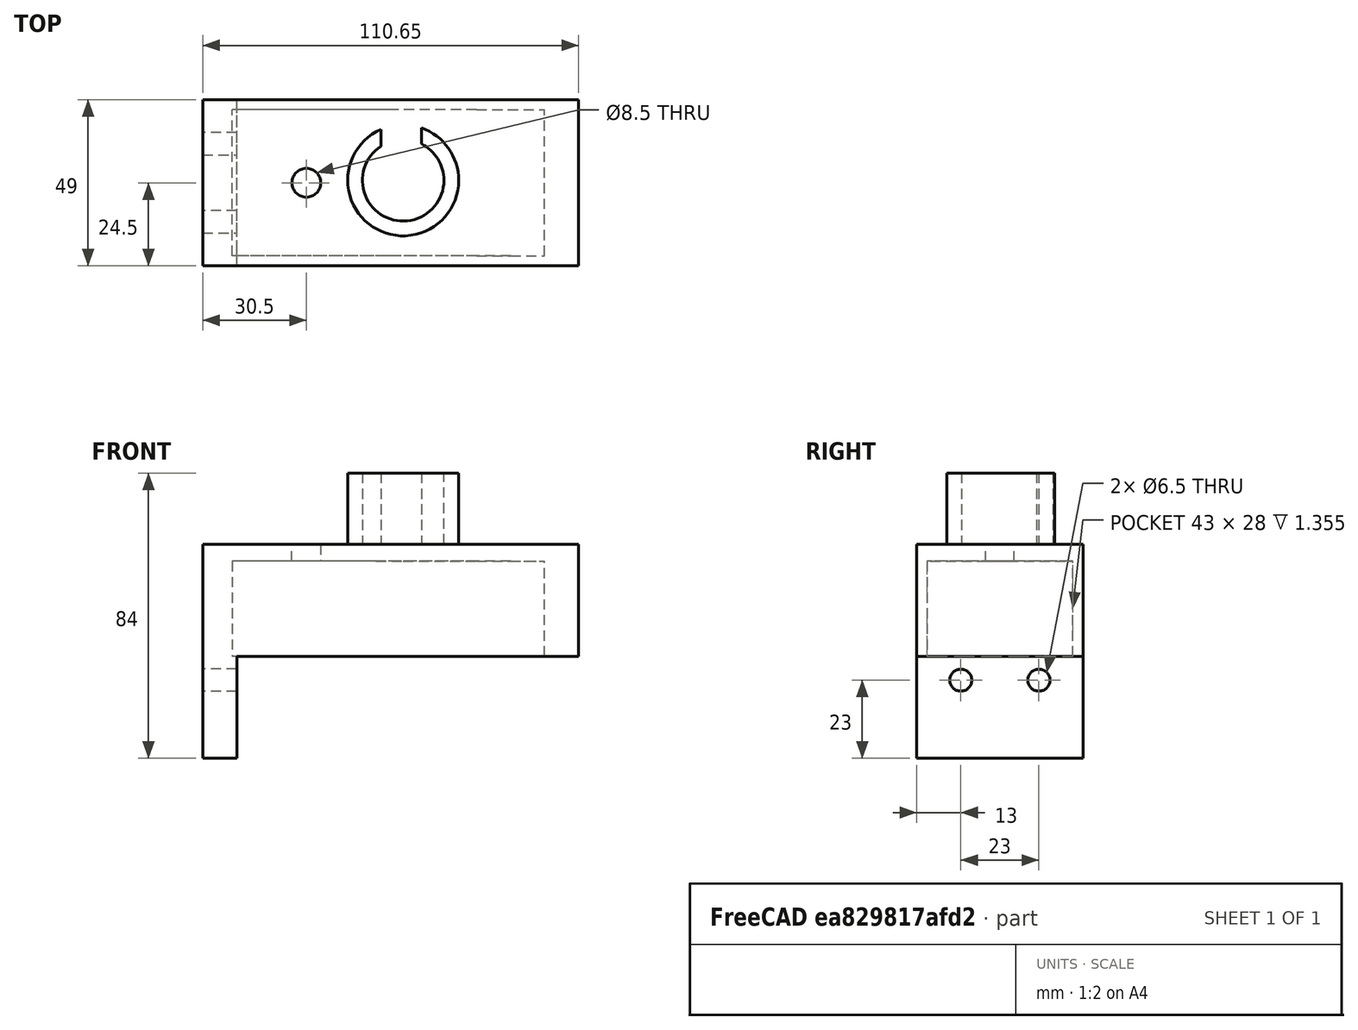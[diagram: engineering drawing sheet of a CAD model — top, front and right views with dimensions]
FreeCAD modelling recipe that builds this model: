
FCSTD DOCUMENT  (FreeCAD 0.18R4 (GitTag))
Label: Caja para engranes 1
License: All rights reserved
LicenseURL: http://en.wikipedia.org/wiki/All_rights_reserved
objects: Sketcher::SketchObject×23, PartDesign::Pad×9, PartDesign::Pocket×9, PartDesign::Body×1
note: 60 computed .brp shape members not serialized (recipe doc carries the construction recipe); baked Part::Feature solids carry a one-line shape summary decoded from their .brp

FEATURE [Sketcher::SketchObject] Sketch
  MapMode = 5
  Support = -> [XY_Plane]
  sketch-geometry (4):
    g0: LineSegment StartX=0 StartY=0 StartZ=0 EndX=49 EndY=0 EndZ=0
    g1: LineSegment StartX=49 StartY=0 StartZ=0 EndX=49 EndY=49 EndZ=0
    g2: LineSegment StartX=49 StartY=49 StartZ=0 EndX=0 EndY=49 EndZ=0
    g3: LineSegment StartX=0 StartY=49 StartZ=0 EndX=0 EndY=0 EndZ=0
  constraints (11):
    c: Coincident(g0,g1)
    c: Coincident(g1,g2)
    c: Coincident(g2,g3)
    c: Coincident(g3,g0)
    c: Horizontal(g0)
    c: Horizontal(g2)
    c: Vertical(g1)
    c: Vertical(g3)
    c: DistanceX(g0,g0) = 49
    c: DistanceY(g1,g1) = 49
    c: Coincident(g0,g-1)
FEATURE [PartDesign::Pad] Pad
  Length = 33
  Length2 = 100
  Profile = -> Sketch
  Type = 0
  expr: Length = 28 + 5
FEATURE [Sketcher::SketchObject] Sketch001
  ExternalGeometry = -> [Pad]
  MapMode = 5
  Placement = pos=(0,0,0) rot=(1,0,0;3.14159rad)
  Support = -> [Pad]
  sketch-geometry (6):
    g0: LineSegment StartX=45 StartY=-4 StartZ=0 EndX=4 EndY=-4 EndZ=0
    g1: LineSegment StartX=4 StartY=-4 StartZ=0 EndX=4 EndY=-45 EndZ=0
    g2: LineSegment StartX=4 StartY=-45 StartZ=0 EndX=45 EndY=-45 EndZ=0
    g3: LineSegment StartX=45 StartY=-45 StartZ=0 EndX=45 EndY=-4 EndZ=0
    g4: Circle [constr] CenterX=24.5 CenterY=-24.5 CenterZ=0 NormalX=0 NormalY=0 NormalZ=1 AngleXU=0 Radius=28.9914
    g5: Circle [constr] CenterX=24.5 CenterY=-24.5 CenterZ=0 NormalX=0 NormalY=0 NormalZ=1 AngleXU=0 Radius=34.6482
  constraints (17):
    c: Coincident(g0,g1)
    c: Coincident(g1,g2)
    c: Coincident(g2,g3)
    c: Coincident(g3,g0)
    c: Equal(g0,g1)
    c: Equal(g0,g2)
    c: Equal(g0,g3)
    c: PointOnObject(g0,g4)
    c: PointOnObject(g1,g4)
    c: PointOnObject(g2,g4)
    c: PointOnObject(g3,g4)
    c: Vertical(g3)
    c: DistanceX(g2,g2) = 41
    c: PointOnObject(g-4,g5)
    c: PointOnObject(g-3,g5)
    c: PointOnObject(g-1,g5)
    c: Coincident(g5,g4)
FEATURE [PartDesign::Pocket] Pocket
  BaseFeature = -> Pad
  Length = 28
  Length2 = 100
  Profile = -> Sketch001
  Type = 0
FEATURE [Sketcher::SketchObject] Sketch004
  MapMode = 5
  Placement = pos=(0,0,33) rot=(0,0,1;0rad)
  sketch-geometry (2):
    g0: Circle [constr] CenterX=24.5 CenterY=24.5 CenterZ=0 NormalX=0 NormalY=0 NormalZ=1 AngleXU=0 Radius=34.6482
    g1: Circle CenterX=24.5 CenterY=24.5 CenterZ=0 NormalX=0 NormalY=0 NormalZ=1 AngleXU=0 Radius=4.25
  constraints (2):
    c: PointOnObject(g-1,g0)
    c: Radius(g1) = 4.25
FEATURE [PartDesign::Pocket] Pocket002
  BaseFeature = -> Pocket
  Length = 5
  Length2 = 100
  Profile = -> Sketch004
  Type = 0
FEATURE [Sketcher::SketchObject] Sketch006
  MapMode = 5
  Placement = pos=(0,0,0) rot=(1,0,0;3.14159rad)
  sketch-geometry (4):
    g0: LineSegment StartX=0 StartY=0 StartZ=0 EndX=4 EndY=0 EndZ=0
    g1: LineSegment StartX=4 StartY=0 StartZ=0 EndX=4 EndY=-49 EndZ=0
    g2: LineSegment StartX=4 StartY=-49 StartZ=0 EndX=0 EndY=-49 EndZ=0
    g3: LineSegment StartX=0 StartY=-49 StartZ=0 EndX=0 EndY=0 EndZ=0
  constraints (10):
    c: Coincident(g0,g1)
    c: Coincident(g1,g2)
    c: Coincident(g2,g3)
    c: Coincident(g3,g0)
    c: Horizontal(g0)
    c: Horizontal(g2)
    c: Vertical(g1)
    c: Vertical(g3)
    c: DistanceY(g3,g3) = 49
    c: Coincident(g0,g-1)
FEATURE [PartDesign::Pad] Pad001
  BaseFeature = -> Pocket002
  Length = 36
  Length2 = 100
  Profile = -> Sketch006
  Type = 0
FEATURE [Sketcher::SketchObject] Sketch007
  ExternalGeometry = -> [Pad001]
  MapMode = 5
  Placement = pos=(49,0,0) rot=(0.57735,0.57735,0.57735;2.0944rad)
  Support = -> [Pad001]
  sketch-geometry (4):
    g0: LineSegment StartX=0 StartY=0 StartZ=0 EndX=49 EndY=0 EndZ=0
    g1: LineSegment StartX=49 StartY=0 StartZ=0 EndX=49 EndY=33 EndZ=0
    g2: LineSegment StartX=49 StartY=33 StartZ=0 EndX=0 EndY=33 EndZ=0
    g3: LineSegment StartX=0 StartY=33 StartZ=0 EndX=0 EndY=0 EndZ=0
  constraints (8):
    c: Coincident(g0,g1)
    c: Coincident(g1,g2)
    c: Coincident(g2,g3)
    c: Coincident(g3,g0)
    c: Horizontal(g0)
    c: Horizontal(g2)
    c: Vertical(g1)
    c: Vertical(g3)
FEATURE [PartDesign::Pad] Pad002
  BaseFeature = -> Pad001
  Length = 49
  Length2 = 100
  Profile = -> Sketch007
  Type = 0
FEATURE [Sketcher::SketchObject] Sketch008
  ExternalGeometry = -> [Pad002]
  MapMode = 5
  Placement = pos=(0,0,0) rot=(1,0,0;3.14159rad)
  Support = -> [Pad002]
  sketch-geometry (6):
    g0: Circle [constr] CenterX=73.5 CenterY=-24.5 CenterZ=0 NormalX=0 NormalY=0 NormalZ=1 AngleXU=0 Radius=34.6482
    g1: LineSegment StartX=94 StartY=-4 StartZ=0 EndX=53 EndY=-4 EndZ=0
    g2: LineSegment StartX=53 StartY=-4 StartZ=0 EndX=53 EndY=-45 EndZ=0
    g3: LineSegment StartX=53 StartY=-45 StartZ=0 EndX=94 EndY=-45 EndZ=0
    g4: LineSegment StartX=94 StartY=-45 StartZ=0 EndX=94 EndY=-4 EndZ=0
    g5: Circle [constr] CenterX=73.5 CenterY=-24.5 CenterZ=0 NormalX=0 NormalY=0 NormalZ=1 AngleXU=0 Radius=28.9914
  constraints (17):
    c: PointOnObject(g-3,g0)
    c: PointOnObject(g-3,g0)
    c: PointOnObject(g-4,g0)
    c: Coincident(g1,g2)
    c: Coincident(g2,g3)
    c: Coincident(g3,g4)
    c: Coincident(g4,g1)
    c: Equal(g1,g2)
    c: Equal(g1,g3)
    c: Equal(g1,g4)
    c: PointOnObject(g1,g5)
    c: PointOnObject(g2,g5)
    c: PointOnObject(g3,g5)
    c: PointOnObject(g4,g5)
    c: Vertical(g4)
    c: Coincident(g0,g5)
    c: DistanceX(g3,g3) = 41
FEATURE [PartDesign::Pocket] Pocket003
  BaseFeature = -> Pad002
  Length = 28
  Length2 = 100
  Profile = -> Sketch008
  Type = 0
FEATURE [Sketcher::SketchObject] Sketch009
  ExternalGeometry = -> [Pocket003]
  MapMode = 5
  Placement = pos=(0,0,0) rot=(1,0,0;3.14159rad)
  Support = -> [Pocket003]
  sketch-geometry (4):
    g0: LineSegment StartX=45 StartY=-4 StartZ=0 EndX=53 EndY=-4 EndZ=0
    g1: LineSegment StartX=53 StartY=-4 StartZ=0 EndX=53 EndY=-45 EndZ=0
    g2: LineSegment StartX=53 StartY=-45 StartZ=0 EndX=45 EndY=-45 EndZ=0
    g3: LineSegment StartX=45 StartY=-45 StartZ=0 EndX=45 EndY=-4 EndZ=0
  constraints (10):
    c: Coincident(g0,g1)
    c: Coincident(g1,g2)
    c: Coincident(g2,g3)
    c: Coincident(g3,g0)
    c: Horizontal(g0)
    c: Horizontal(g2)
    c: Vertical(g1)
    c: Vertical(g3)
    c: Coincident(g-3,g0)
    c: Coincident(g1,g-4)
FEATURE [PartDesign::Pocket] Pocket004
  BaseFeature = -> Pocket003
  Length = 28
  Length2 = 100
  Profile = -> Sketch009
  Type = 0
FEATURE [Sketcher::SketchObject] Sketch010
  ExternalGeometry = -> [Pocket004]
  MapMode = 5
  Placement = pos=(0,0,33) rot=(0,0,1;0rad)
  Support = -> [Pocket004]
  sketch-geometry (2):
    g0: Circle [constr] CenterX=73.5 CenterY=24.5 CenterZ=0 NormalX=0 NormalY=0 NormalZ=1 AngleXU=0 Radius=34.6482
    g1: LineSegment [constr] StartX=73.5 StartY=25.8216 StartZ=0 EndX=41.7848 EndY=25.8216 EndZ=0
  constraints (4):
    c: PointOnObject(g-6,g0)
    c: PointOnObject(g-5,g0)
    c: PointOnObject(g-6,g0)
    c: Horizontal(g1)
FEATURE [Sketcher::SketchObject] Sketch011
  ExternalGeometry = -> [Pocket004]
  MapMode = 5
  Placement = pos=(0,0,33) rot=(0,0,1;0rad)
  Support = -> [Pocket004]
  expr: Constraints[4] = 49 / 2
  expr: Constraints[0] = 24 / 2
  sketch-geometry (4):
    g0: Circle CenterX=53 CenterY=25.204 CenterZ=0 NormalX=0 NormalY=0 NormalZ=1 AngleXU=0 Radius=12
    g1: Circle CenterX=53 CenterY=25.204 CenterZ=0 NormalX=0 NormalY=0 NormalZ=1 AngleXU=0 Radius=16.3474
    g2: LineSegment StartX=49 StartY=49.704 StartZ=0 EndX=49 EndY=25.204 EndZ=0
    g3: LineSegment [constr] StartX=49 StartY=25.204 StartZ=0 EndX=53 EndY=25.204 EndZ=0
  constraints (9):
    c: Radius(g0) = 12
    c: PointOnObject(g2,g-3)
    c: Coincident(g1,g0)
    c: Vertical(g2)
    c: DistanceY(g2,g2) = 24.5
    c: DistanceX(g3,g3) = 4
    c: Coincident(g3,g2)
    c: Horizontal(g3)
    c: Coincident(g0,g3)
FEATURE [PartDesign::Pad] Pad003
  BaseFeature = -> Pocket004
  Length = 21
  Length2 = 100
  Profile = -> Sketch011
  Type = 0
FEATURE [Sketcher::SketchObject] Sketch012
  ExternalGeometry = -> [Pad003]
  MapMode = 5
  Placement = pos=(0,0,33) rot=(0,0,1;0rad)
  Support = -> [Pad003]
  sketch-geometry (5):
    g0: LineSegment StartX=58.3651 StartY=43.154 StartZ=0 EndX=46.4651 EndY=43.154 EndZ=0
    g1: LineSegment StartX=46.4651 StartY=43.154 StartZ=0 EndX=46.4651 EndY=31.254 EndZ=0
    g2: LineSegment StartX=46.4651 StartY=31.254 StartZ=0 EndX=58.3651 EndY=31.254 EndZ=0
    g3: LineSegment StartX=58.3651 StartY=31.254 StartZ=0 EndX=58.3651 EndY=43.154 EndZ=0
    g4: Circle [constr] CenterX=52.4151 CenterY=37.204 CenterZ=0 NormalX=0 NormalY=0 NormalZ=1 AngleXU=0 Radius=8.41457
  constraints (14):
    c: Coincident(g0,g1)
    c: Coincident(g1,g2)
    c: Coincident(g2,g3)
    c: Coincident(g3,g0)
    c: Equal(g0,g1)
    c: Equal(g0,g2)
    c: Equal(g0,g3)
    c: PointOnObject(g0,g4)
    c: PointOnObject(g1,g4)
    c: PointOnObject(g2,g4)
    c: PointOnObject(g3,g4)
    c: Horizontal(g0)
    c: DistanceX(g0,g0) = 11.9
    c: DistanceY(g-3,g4) = 12
FEATURE [Sketcher::SketchObject] Sketch013
  MapMode = 5
  Placement = pos=(0,0,33) rot=(0,0,1;0rad)
  Support = -> [Pad003]
FEATURE [PartDesign::Pocket] Pocket005
  BaseFeature = -> Pad003
  Length = 22
  Length2 = 100
  Profile = -> Sketch012
  Reversed = true
  Type = 0
FEATURE [Sketcher::SketchObject] Sketch014
  MapMode = 5
  Placement = pos=(0,0,0) rot=(1,0,0;3.14159rad)
  Support = -> [Pocket005]
FEATURE [Sketcher::SketchObject] Sketch015
  ExternalGeometry = -> [Pocket005]
  MapMode = 5
  Placement = pos=(0,0,0) rot=(0.57735,-0.57735,-0.57735;2.0944rad)
  Support = -> [Pocket005]
  sketch-geometry (4):
    g0: LineSegment StartX=-49 StartY=-36 StartZ=0 EndX=0 EndY=-36 EndZ=0
    g1: LineSegment StartX=0 StartY=-36 StartZ=0 EndX=0 EndY=0 EndZ=0
    g2: LineSegment StartX=0 StartY=0 StartZ=0 EndX=-49 EndY=0 EndZ=0
    g3: LineSegment StartX=-49 StartY=0 StartZ=0 EndX=-49 EndY=-36 EndZ=0
  constraints (8):
    c: Coincident(g0,g1)
    c: Coincident(g1,g2)
    c: Coincident(g2,g3)
    c: Coincident(g3,g0)
    c: Horizontal(g0)
    c: Horizontal(g2)
    c: Vertical(g1)
    c: Vertical(g3)
FEATURE [PartDesign::Pocket] Pocket006
  BaseFeature = -> Pocket005
  Length = 4
  Length2 = 100
  Profile = -> Sketch015
  Type = 0
FEATURE [Sketcher::SketchObject] Sketch016
  ExternalGeometry = -> [Pocket006]
  MapMode = 5
  Placement = pos=(0,0,0) rot=(1,0,0;3.14159rad)
  Support = -> [Pocket006]
  sketch-geometry (8):
    g0: LineSegment StartX=4 StartY=-49 StartZ=0 EndX=-6 EndY=-49 EndZ=0
    g1: LineSegment StartX=-6 StartY=-49 StartZ=0 EndX=-6 EndY=0 EndZ=0
    g2: LineSegment StartX=-6 StartY=0 StartZ=0 EndX=4 EndY=0 EndZ=0
    g3: LineSegment StartX=4 StartY=0 StartZ=0 EndX=4 EndY=-49 EndZ=0
    g4: LineSegment StartX=104 StartY=-49 StartZ=0 EndX=94 EndY=-49 EndZ=0
    g5: LineSegment StartX=94 StartY=-49 StartZ=0 EndX=94 EndY=7.1e-15 EndZ=0
    g6: LineSegment StartX=94 StartY=4.4e-15 StartZ=0 EndX=104 EndY=4.4e-15 EndZ=0
    g7: LineSegment StartX=104 StartY=4.4e-15 StartZ=0 EndX=104 EndY=-49 EndZ=0
  constraints (23):
    c: Coincident(g0,g1)
    c: Coincident(g1,g2)
    c: Coincident(g2,g3)
    c: Coincident(g3,g0)
    c: Horizontal(g0)
    c: Horizontal(g2)
    c: Vertical(g1)
    c: Vertical(g3)
    c: Coincident(g0,g-3)
    c: PointOnObject(g-1,g2)
    c: DistanceX(g0,g0) = 10
    c: Coincident(g4,g5)
    c: Coincident(g5,g6)
    c: Coincident(g6,g7)
    c: Coincident(g7,g4)
    c: Horizontal(g4)
    c: Horizontal(g6)
    c: Vertical(g5)
    c: Vertical(g7)
    c: PointOnObject(g-7,g5)
    c: PointOnObject(g4,g-5)
    c: DistanceX(g6,g6) = 10
    c: PointOnObject(g-6,g6)
FEATURE [PartDesign::Pad] Pad004
  BaseFeature = -> Pocket006
  Length = 33
  Length2 = 100
  Profile = -> Sketch016
  Reversed = true
  Type = 0
FEATURE [Sketcher::SketchObject] CopySketch017
  Placement = pos=(0,0,0) rot=(1,0,0;3.14159rad)
  sketch-geometry (4):
    g0: LineSegment StartX=104 StartY=7.1e-15 StartZ=0 EndX=74.6453 EndY=7.1e-15 EndZ=0
    g1: LineSegment StartX=74.6453 StartY=7.1e-15 StartZ=0 EndX=74.6453 EndY=-49 EndZ=0
    g2: LineSegment StartX=74.6453 StartY=-49 StartZ=0 EndX=104 EndY=-49 EndZ=0
    g3: LineSegment StartX=104 StartY=-49 StartZ=0 EndX=104 EndY=7.1e-15 EndZ=0
  constraints (8):
    c: Coincident(g0,g1)
    c: Coincident(g1,g2)
    c: Coincident(g2,g3)
    c: Coincident(g3,g0)
    c: Horizontal(g0)
    c: Horizontal(g2)
    c: Vertical(g1)
    c: Vertical(g3)
FEATURE [PartDesign::Pocket] Pocket007
  BaseFeature = -> Pad004
  Length = 35
  Length2 = 100
  Profile = -> CopySketch017
  Type = 0
FEATURE [Sketcher::SketchObject] Sketch017
  ExternalGeometry = -> [Pocket007]
  MapMode = 5
  Placement = pos=(74.6453,0,0) rot=(0.57735,0.57735,0.57735;2.0944rad)
  Support = -> [Pocket007]
  sketch-geometry (4):
    g0: LineSegment StartX=0 StartY=0 StartZ=0 EndX=45 EndY=0 EndZ=0
    g1: LineSegment StartX=45 StartY=0 StartZ=0 EndX=45 EndY=28 EndZ=0
    g2: LineSegment StartX=45 StartY=28 StartZ=0 EndX=0 EndY=28 EndZ=0
    g3: LineSegment StartX=0 StartY=28 StartZ=0 EndX=0 EndY=0 EndZ=0
  constraints (9):
    c: Coincident(g0,g1)
    c: Coincident(g1,g2)
    c: Coincident(g2,g3)
    c: Coincident(g3,g0)
    c: Horizontal(g0)
    c: Horizontal(g2)
    c: Vertical(g1)
    c: Vertical(g3)
    c: Coincident(g1,g-3)
FEATURE [PartDesign::Pad] Pad005
  BaseFeature = -> Pocket007
  Length = 10
  Length2 = 100
  Profile = -> Sketch017
  Type = 0
FEATURE [Sketcher::SketchObject] Sketch018
  ExternalGeometry = -> [Pad005]
  MapMode = 5
  Placement = pos=(0,0,0) rot=(1,0,0;3.14159rad)
  Support = -> [Pad005]
  sketch-geometry (4):
    g0: LineSegment StartX=-6 StartY=0 StartZ=0 EndX=4 EndY=0 EndZ=0
    g1: LineSegment StartX=4 StartY=0 StartZ=0 EndX=4 EndY=-49 EndZ=0
    g2: LineSegment StartX=4 StartY=-49 StartZ=0 EndX=-6 EndY=-49 EndZ=0
    g3: LineSegment StartX=-6 StartY=-49 StartZ=0 EndX=-6 EndY=0 EndZ=0
  constraints (10):
    c: Coincident(g0,g1)
    c: Coincident(g1,g2)
    c: Coincident(g2,g3)
    c: Coincident(g3,g0)
    c: Horizontal(g0)
    c: Horizontal(g2)
    c: Vertical(g1)
    c: Vertical(g3)
    c: Coincident(g1,g-4)
    c: Coincident(g0,g-3)
FEATURE [PartDesign::Pad] Pad006
  BaseFeature = -> Pad005
  Length = 30
  Length2 = 100
  Profile = -> Sketch018
  Type = 0
FEATURE [Sketcher::SketchObject] Sketch019
  ExternalGeometry = -> [Pad006]
  MapMode = 5
  Placement = pos=(84.6453,0,0) rot=(0.57735,0.57735,0.57735;2.0944rad)
  Support = -> [Pad006]
  sketch-geometry (8):
    g0: LineSegment StartX=46 StartY=0 StartZ=0 EndX=49 EndY=0 EndZ=0
    g1: LineSegment StartX=46 StartY=0 StartZ=0 EndX=46 EndY=28 EndZ=0
    g2: LineSegment StartX=49 StartY=0 StartZ=0 EndX=49 EndY=33 EndZ=0
    g3: LineSegment StartX=49 StartY=33 StartZ=0 EndX=-7.1e-15 EndY=33 EndZ=0
    g4: LineSegment StartX=-7.1e-15 StartY=33 StartZ=0 EndX=0 EndY=0 EndZ=0
    g5: LineSegment StartX=0 StartY=0 StartZ=0 EndX=3 EndY=0 EndZ=0
    g6: LineSegment StartX=3 StartY=0 StartZ=0 EndX=3 EndY=28 EndZ=0
    g7: LineSegment StartX=3 StartY=28 StartZ=0 EndX=46 EndY=28 EndZ=0
  constraints (20):
    c: DistanceX(g0,g0) = 3
    c: Coincident(g0,g-5)
    c: DistanceY(g1,g1) = 28
    c: Coincident(g1,g0)
    c: DistanceX(g-6,g1) = 1
    c: Horizontal(g0)
    c: Coincident(g0,g2)
    c: Coincident(g-3,g2)
    c: Coincident(g3,g-3)
    c: Coincident(g3,g2)
    c: Coincident(g4,g3)
    c: Coincident(g4,g-1)
    c: Horizontal(g5)
    c: Coincident(g5,g4)
    c: DistanceX(g5,g5) = 3
    c: Vertical(g6)
    c: Coincident(g6,g5)
    c: DistanceY(g6,g6) = 28
    c: Coincident(g7,g6)
    c: Coincident(g7,g1)
FEATURE [Sketcher::SketchObject] CopySketch019
  Placement = pos=(84.6453,0,0) rot=(0.57735,0.57735,0.57735;2.0944rad)
  sketch-geometry (8):
    g0: LineSegment StartX=46 StartY=0 StartZ=0 EndX=49 EndY=0 EndZ=0
    g1: LineSegment StartX=46 StartY=0 StartZ=0 EndX=46 EndY=28 EndZ=0
    g2: LineSegment StartX=49 StartY=0 StartZ=0 EndX=49 EndY=33 EndZ=0
    g3: LineSegment StartX=49 StartY=33 StartZ=0 EndX=-7.1e-15 EndY=33 EndZ=0
    g4: LineSegment StartX=-7.1e-15 StartY=33 StartZ=0 EndX=0 EndY=0 EndZ=0
    g5: LineSegment StartX=0 StartY=0 StartZ=0 EndX=3 EndY=0 EndZ=0
    g6: LineSegment StartX=3 StartY=0 StartZ=0 EndX=3 EndY=28 EndZ=0
    g7: LineSegment StartX=3 StartY=28 StartZ=0 EndX=46 EndY=28 EndZ=0
  constraints (16):
    c: DistanceX(g0,g0) = 3
    c: DistanceY(g1,g1) = 28
    c: Coincident(g1,g0)
    c: Horizontal(g0)
    c: Coincident(g0,g2)
    c: Coincident(g3,g2)
    c: Coincident(g4,g3)
    c: Coincident(g4,g-1)
    c: Horizontal(g5)
    c: Coincident(g5,g4)
    c: DistanceX(g5,g5) = 3
    c: Vertical(g6)
    c: Coincident(g6,g5)
    c: DistanceY(g6,g6) = 28
    c: Coincident(g7,g6)
    c: Coincident(g7,g1)
FEATURE [PartDesign::Pad] Pad007
  BaseFeature = -> Pad006
  Length = 20
  Length2 = 100
  Midplane = true
  Profile = -> CopySketch019
  Reversed = true
  Type = 0
FEATURE [Sketcher::SketchObject] Sketch020
  MapMode = 5
  Placement = pos=(0,0,0) rot=(1,0,0;3.14159rad)
  Support = -> [Pad007]
FEATURE [Sketcher::SketchObject] Sketch021
  ExternalGeometry = -> [Pad007]
  MapMode = 5
  Placement = pos=(94.6453,0,0) rot=(0.57735,0.57735,0.57735;2.0944rad)
  Support = -> [Pad007]
  sketch-geometry (4):
    g0: LineSegment StartX=3 StartY=0 StartZ=0 EndX=46 EndY=0 EndZ=0
    g1: LineSegment StartX=46 StartY=0 StartZ=0 EndX=46 EndY=28 EndZ=0
    g2: LineSegment StartX=46 StartY=28 StartZ=0 EndX=3 EndY=28 EndZ=0
    g3: LineSegment StartX=3 StartY=28 StartZ=0 EndX=3 EndY=0 EndZ=0
  constraints (10):
    c: Coincident(g0,g1)
    c: Coincident(g1,g2)
    c: Coincident(g2,g3)
    c: Coincident(g3,g0)
    c: Horizontal(g0)
    c: Horizontal(g2)
    c: Vertical(g1)
    c: Vertical(g3)
    c: Coincident(g0,g-4)
    c: Coincident(g1,g-3)
FEATURE [PartDesign::Pocket] Pocket008
  BaseFeature = -> Pad007
  Length = 92
  Length2 = 100
  Profile = -> Sketch021
  Type = 0
FEATURE [Sketcher::SketchObject] Sketch022
  ExternalGeometry = -> [Pocket008]
  MapMode = 5
  Placement = pos=(-6,0,0) rot=(0.57735,-0.57735,-0.57735;2.0944rad)
  Support = -> [Pocket008]
  expr: Constraints[3] = 6.5 / 2
  expr: Constraints[0] = 6.5 / 2
  sketch-geometry (2):
    g0: Circle CenterX=-36 CenterY=-7 CenterZ=0 NormalX=0 NormalY=0 NormalZ=1 AngleXU=0 Radius=3.25
    g1: Circle CenterX=-13 CenterY=-7 CenterZ=0 NormalX=0 NormalY=0 NormalZ=1 AngleXU=0 Radius=3.25
  constraints (6):
    c: Radius(g0) = 3.25
    c: DistanceX(g-4,g0) = 13
    c: DistanceY(g-4,g0) = 23
    c: Radius(g1) = 3.25
    c: DistanceX(g1,g-3) = 13
    c: DistanceY(g-3,g1) = 23
FEATURE [PartDesign::Pocket] Pocket009
  BaseFeature = -> Pocket008
  Length = 10
  Length2 = 100
  Profile = -> Sketch022
  Type = 0
FEATURE [Sketcher::SketchObject] Sketch023
  ExternalGeometry = -> [Pocket009]
  MapMode = 5
  Placement = pos=(94.6453,0,0) rot=(0.57735,0.57735,0.57735;2.0944rad)
  Support = -> [Pocket009]
  sketch-geometry (4):
    g0: LineSegment StartX=0 StartY=0 StartZ=0 EndX=49 EndY=0 EndZ=0
    g1: LineSegment StartX=49 StartY=0 StartZ=0 EndX=49 EndY=33 EndZ=0
    g2: LineSegment StartX=49 StartY=33 StartZ=0 EndX=0 EndY=33 EndZ=0
    g3: LineSegment StartX=0 StartY=33 StartZ=0 EndX=0 EndY=0 EndZ=0
  constraints (10):
    c: Coincident(g0,g1)
    c: Coincident(g1,g2)
    c: Coincident(g2,g3)
    c: Coincident(g3,g0)
    c: Horizontal(g0)
    c: Horizontal(g2)
    c: Vertical(g1)
    c: Vertical(g3)
    c: Coincident(g1,g-3)
    c: Coincident(g0,g-1)
FEATURE [PartDesign::Pad] Pad008
  BaseFeature = -> Pocket009
  Length = 10
  Length2 = 100
  Profile = -> Sketch023
  Type = 0
FEATURE [PartDesign::Body] Body
  Group = -> [Sketch,Pad,Sketch001,Pocket,Sketch004,Pocket002,Sketch006,Pad001,Sketch007,Pad002,Sketch008,Pocket003,Sketch009,Pocket004,Sketch010,Sketch011,Pad003,Sketch012,Sketch013,Pocket005,Sketch014,Sketch015,Pocket006,Sketch016,Pad004,Pocket007,Sketch017,Pad005,Sketch018,Pad006,Pad007,Sketch020,Sketch021,Pocket008,Sketch022,Pocket009,Sketch023,Pad008]
  Origin = -> Origin
  Tip = -> Pad008
